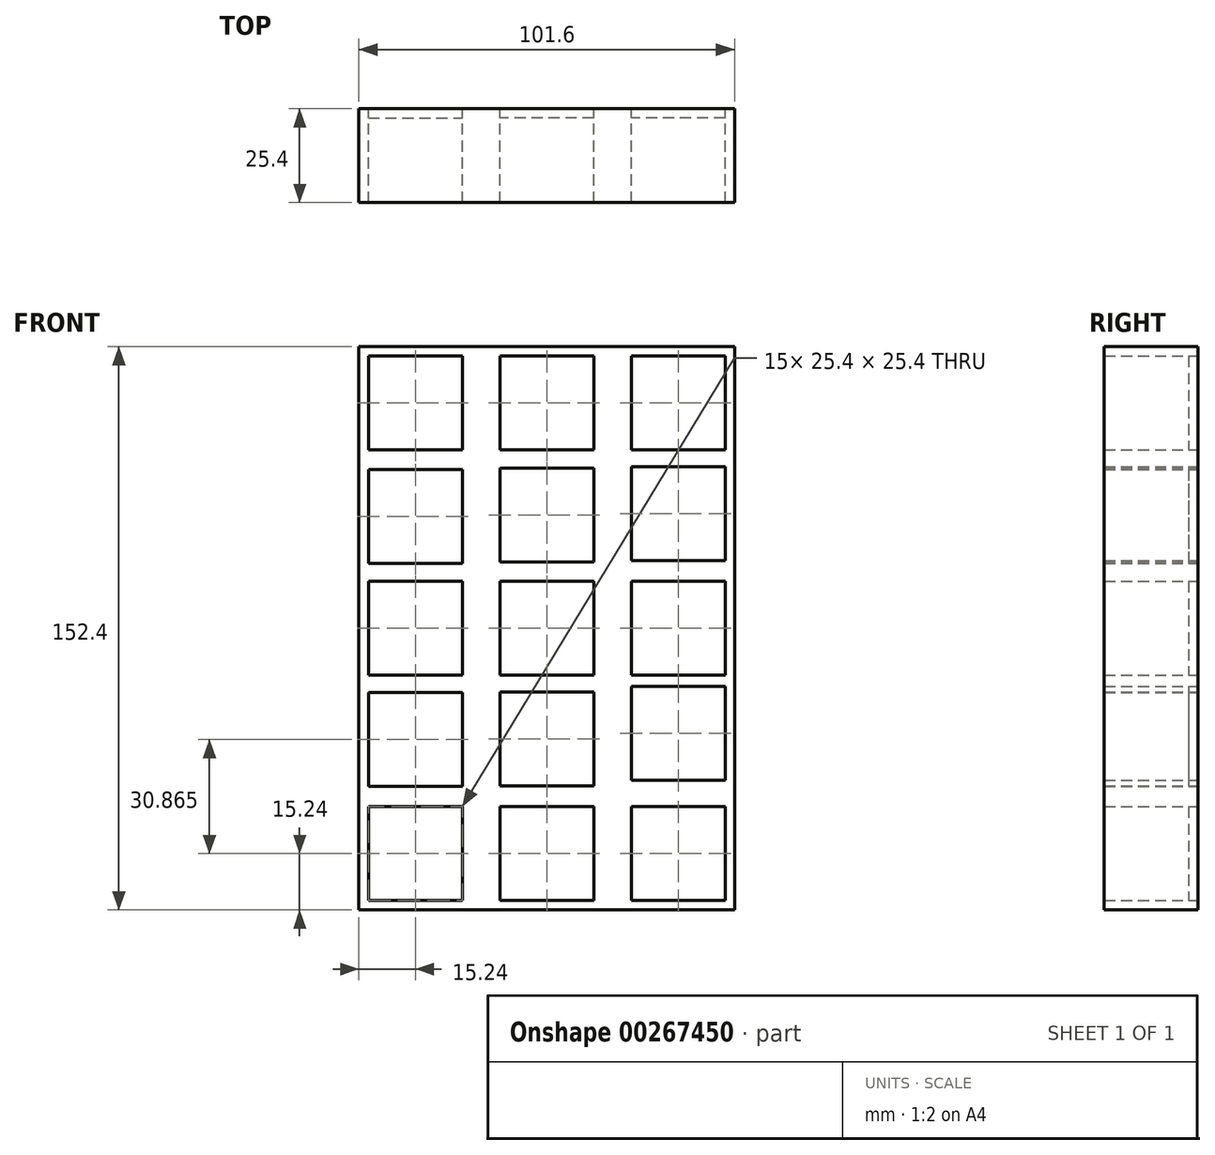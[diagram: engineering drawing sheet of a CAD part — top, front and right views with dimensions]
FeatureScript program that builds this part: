
annotation { "Feature Type Name" : "Feature", "Feature Type Description" : "" }
export const myFeature = defineFeature(function(context is Context, id is Id, definition is map)
    precondition{}
    {
        {
            var Q0;
            Q0=qCreatedBy(makeId("Front.planeOp"),FACE);
            var sketch = newSketch(context, id + "F0", { "sketchPlane" : qUnion([Q0])});
            skLineSegment(sketch, "E0.bottom", {"start": v(50.8, 76.2) * mm, "end": v(-50.8, 76.2) * mm});
            skLineSegment(sketch, "E0.top", {"start": v(50.8, -76.2) * mm, "end": v(-50.8, -76.2) * mm});
            skLineSegment(sketch, "E0.left", {"start": v(50.8, 76.2) * mm, "end": v(50.8, -76.2) * mm});
            skLineSegment(sketch, "E0.right", {"start": v(-50.8, 76.2) * mm, "end": v(-50.8, -76.2) * mm});
            skPoint(sketch, "E0.middle", {"position": v(0, 0) * mm});
            skLineSegment(sketch, "E1.bottom", {"start": v(48.26, 73.66) * mm, "end": v(-48.26, 73.66) * mm});
            skLineSegment(sketch, "E1.top", {"start": v(48.26, -73.66) * mm, "end": v(-48.26, -73.66) * mm});
            skLineSegment(sketch, "E1.left", {"start": v(48.26, 73.66) * mm, "end": v(48.26, -73.66) * mm});
            skLineSegment(sketch, "E1.right", {"start": v(-48.26, 73.66) * mm, "end": v(-48.26, -73.66) * mm});
            skLineSegment(sketch, "E2.bottom", {"start": v(-48.26, 73.66) * mm, "end": v(-22.86, 73.66) * mm});
            skLineSegment(sketch, "E2.top", {"start": v(-48.26, 48.26) * mm, "end": v(-22.86, 48.26) * mm});
            skLineSegment(sketch, "E2.left", {"start": v(-48.26, 73.66) * mm, "end": v(-48.26, 48.26) * mm});
            skLineSegment(sketch, "E2.right", {"start": v(-22.86, 73.66) * mm, "end": v(-22.86, 48.26) * mm});
            skLineSegment(sketch, "E3.bottom", {"start": v(48.26, 73.66) * mm, "end": v(22.86, 73.66) * mm});
            skLineSegment(sketch, "E3.top", {"start": v(48.26, 48.26) * mm, "end": v(22.86, 48.26) * mm});
            skLineSegment(sketch, "E3.left", {"start": v(48.26, 73.66) * mm, "end": v(48.26, 48.26) * mm});
            skLineSegment(sketch, "E3.right", {"start": v(22.86, 73.66) * mm, "end": v(22.86, 48.26) * mm});
            skLineSegment(sketch, "E4", {"start": v(0, 73.66) * mm, "end": v(0, 60.96) * mm});
            skPoint(sketch, "E4.endSnap0", {"position": v(0, 73.66) * mm});
            skLineSegment(sketch, "E5.bottom", {"start": v(12.7, 73.66) * mm, "end": v(-12.7, 73.66) * mm});
            skLineSegment(sketch, "E5.top", {"start": v(12.7, 48.26) * mm, "end": v(-12.7, 48.26) * mm});
            skLineSegment(sketch, "E5.left", {"start": v(12.7, 73.66) * mm, "end": v(12.7, 48.26) * mm});
            skLineSegment(sketch, "E5.right", {"start": v(-12.7, 73.66) * mm, "end": v(-12.7, 48.26) * mm});
            skPoint(sketch, "E5.middle", {"position": v(0, 60.96) * mm});
            skLineSegment(sketch, "E6", {"start": v(0, -73.66) * mm, "end": v(0, -60.96) * mm});
            skPoint(sketch, "E6.endSnap0", {"position": v(0, -73.66) * mm});
            skLineSegment(sketch, "E7.bottom", {"start": v(12.7, -48.26) * mm, "end": v(-12.7, -48.26) * mm});
            skLineSegment(sketch, "E7.top", {"start": v(12.7, -73.66) * mm, "end": v(-12.7, -73.66) * mm});
            skLineSegment(sketch, "E7.left", {"start": v(12.7, -48.26) * mm, "end": v(12.7, -73.66) * mm});
            skLineSegment(sketch, "E7.right", {"start": v(-12.7, -48.26) * mm, "end": v(-12.7, -73.66) * mm});
            skPoint(sketch, "E7.middle", {"position": v(0, -60.96) * mm});
            skLineSegment(sketch, "E8.bottom", {"start": v(-48.26, -73.66) * mm, "end": v(-22.86, -73.66) * mm});
            skLineSegment(sketch, "E8.top", {"start": v(-48.26, -48.26) * mm, "end": v(-22.86, -48.26) * mm});
            skLineSegment(sketch, "E8.left", {"start": v(-48.26, -73.66) * mm, "end": v(-48.26, -48.26) * mm});
            skLineSegment(sketch, "E8.right", {"start": v(-22.86, -73.66) * mm, "end": v(-22.86, -48.26) * mm});
            skLineSegment(sketch, "E9.bottom", {"start": v(48.26, -73.66) * mm, "end": v(22.86, -73.66) * mm});
            skLineSegment(sketch, "E9.top", {"start": v(48.26, -48.26) * mm, "end": v(22.86, -48.26) * mm});
            skLineSegment(sketch, "E9.left", {"start": v(48.26, -73.66) * mm, "end": v(48.26, -48.26) * mm});
            skLineSegment(sketch, "E9.right", {"start": v(22.86, -73.66) * mm, "end": v(22.86, -48.26) * mm});
            skLineSegment(sketch, "E10.bottom", {"start": v(12.7, 12.7) * mm, "end": v(-12.7, 12.7) * mm});
            skLineSegment(sketch, "E10.top", {"start": v(12.7, -12.7) * mm, "end": v(-12.7, -12.7) * mm});
            skLineSegment(sketch, "E10.left", {"start": v(12.7, 12.7) * mm, "end": v(12.7, -12.7) * mm});
            skLineSegment(sketch, "E10.right", {"start": v(-12.7, 12.7) * mm, "end": v(-12.7, -12.7) * mm});
            skLineSegment(sketch, "E11", {"start": v(-48.26, 0) * mm, "end": v(-35.56, 0) * mm});
            skLineSegment(sketch, "E12", {"start": v(48.26, 0) * mm, "end": v(35.56, 0) * mm});
            skLineSegment(sketch, "E13.bottom", {"start": v(-48.26, 12.7) * mm, "end": v(-22.86, 12.7) * mm});
            skLineSegment(sketch, "E13.top", {"start": v(-48.26, -12.7) * mm, "end": v(-22.86, -12.7) * mm});
            skLineSegment(sketch, "E13.left", {"start": v(-48.26, 12.7) * mm, "end": v(-48.26, -12.7) * mm});
            skLineSegment(sketch, "E13.right", {"start": v(-22.86, 12.7) * mm, "end": v(-22.86, -12.7) * mm});
            skPoint(sketch, "E13.middle", {"position": v(-35.56, 0) * mm});
            skLineSegment(sketch, "E14.bottom", {"start": v(48.26, 12.7) * mm, "end": v(22.86, 12.7) * mm});
            skLineSegment(sketch, "E14.top", {"start": v(48.26, -12.7) * mm, "end": v(22.86, -12.7) * mm});
            skLineSegment(sketch, "E14.left", {"start": v(48.26, 12.7) * mm, "end": v(48.26, -12.7) * mm});
            skLineSegment(sketch, "E14.right", {"start": v(22.86, 12.7) * mm, "end": v(22.86, -12.7) * mm});
            skPoint(sketch, "E14.middle", {"position": v(35.56, 0) * mm});
            skLineSegment(sketch, "E15", {"start": v(-48.26, 30.25) * mm, "end": v(-35.56, 30.25) * mm});
            skLineSegment(sketch, "E16.bottom", {"start": v(-22.86, 42.95) * mm, "end": v(-48.26, 42.95) * mm});
            skLineSegment(sketch, "E16.top", {"start": v(-22.86, 17.55) * mm, "end": v(-48.26, 17.55) * mm});
            skLineSegment(sketch, "E16.left", {"start": v(-22.86, 42.95) * mm, "end": v(-22.86, 17.55) * mm});
            skLineSegment(sketch, "E16.right", {"start": v(-48.26, 42.95) * mm, "end": v(-48.26, 17.55) * mm});
            skPoint(sketch, "E16.middle", {"position": v(-35.56, 30.25) * mm});
            skLineSegment(sketch, "E17.bottom", {"start": v(48.26, 43.78) * mm, "end": v(22.86, 43.78) * mm});
            skLineSegment(sketch, "E17.top", {"start": v(48.26, 18.38) * mm, "end": v(22.86, 18.38) * mm});
            skLineSegment(sketch, "E17.left", {"start": v(48.26, 43.78) * mm, "end": v(48.26, 18.38) * mm});
            skLineSegment(sketch, "E17.right", {"start": v(22.86, 43.78) * mm, "end": v(22.86, 18.38) * mm});
            skPoint(sketch, "E17.middle", {"position": v(35.56, 31.08) * mm});
            skPoint(sketch, "E18", {"position": v(0, 30.66) * mm});
            skLineSegment(sketch, "E19.bottom", {"start": v(12.7, 43.36) * mm, "end": v(-12.7, 43.36) * mm});
            skLineSegment(sketch, "E19.top", {"start": v(12.7, 17.96) * mm, "end": v(-12.7, 17.96) * mm});
            skLineSegment(sketch, "E19.left", {"start": v(12.7, 43.36) * mm, "end": v(12.7, 17.96) * mm});
            skLineSegment(sketch, "E19.right", {"start": v(-12.7, 43.36) * mm, "end": v(-12.7, 17.96) * mm});
            skPoint(sketch, "E20", {"position": v(0, -29.93) * mm});
            skLineSegment(sketch, "E21.bottom", {"start": v(12.7, -17.23) * mm, "end": v(-12.7, -17.23) * mm});
            skLineSegment(sketch, "E21.top", {"start": v(12.7, -42.63) * mm, "end": v(-12.7, -42.63) * mm});
            skLineSegment(sketch, "E21.left", {"start": v(12.7, -17.23) * mm, "end": v(12.7, -42.63) * mm});
            skLineSegment(sketch, "E21.right", {"start": v(-12.7, -17.23) * mm, "end": v(-12.7, -42.63) * mm});
            skLineSegment(sketch, "E22", {"start": v(-48.26, -30.1) * mm, "end": v(-35.56, -30.1) * mm});
            skLineSegment(sketch, "E23", {"start": v(48.26, -28.44) * mm, "end": v(35.56, -28.44) * mm});
            skLineSegment(sketch, "E24.bottom", {"start": v(-48.26, -17.4) * mm, "end": v(-22.86, -17.4) * mm});
            skLineSegment(sketch, "E24.top", {"start": v(-48.26, -42.8) * mm, "end": v(-22.86, -42.8) * mm});
            skLineSegment(sketch, "E24.left", {"start": v(-48.26, -17.4) * mm, "end": v(-48.26, -42.8) * mm});
            skLineSegment(sketch, "E24.right", {"start": v(-22.86, -17.4) * mm, "end": v(-22.86, -42.8) * mm});
            skPoint(sketch, "E24.middle", {"position": v(-35.56, -30.1) * mm});
            skLineSegment(sketch, "E25.bottom", {"start": v(48.26, -15.74) * mm, "end": v(22.86, -15.74) * mm});
            skLineSegment(sketch, "E25.top", {"start": v(48.26, -41.14) * mm, "end": v(22.86, -41.14) * mm});
            skLineSegment(sketch, "E25.left", {"start": v(48.26, -15.74) * mm, "end": v(48.26, -41.14) * mm});
            skLineSegment(sketch, "E25.right", {"start": v(22.86, -15.74) * mm, "end": v(22.86, -41.14) * mm});
            skPoint(sketch, "E25.middle", {"position": v(35.56, -28.44) * mm});
            skSolve(sketch);
        }
        {
            var Q0;
            Q0=makeQuery(id+"F0.imprint","IMPRINT",FACE,{"disambiguationData":[TD([[makeQuery(id+"F0.imprint","IMPRINT",EDGE,{"derivedFrom":sQuery(id+"F0.wireOp",EDGE,"E2.bottom")}),-1.0]])]});
            var Q1;
            Q1=makeQuery(id+"F0.imprint","IMPRINT",FACE,{"disambiguationData":[TD([[makeQuery(id+"F0.imprint","IMPRINT",EDGE,{"derivedFrom":sQuery(id+"F0.wireOp",EDGE,"E5.top")}),-1.0]])]});
            var Q2;
            Q2=makeQuery(id+"F0.imprint","IMPRINT",FACE,{"disambiguationData":[TD([[makeQuery(id+"F0.imprint","IMPRINT",EDGE,{"derivedFrom":sQuery(id+"F0.wireOp",EDGE,"E3.bottom")}),1.0]])]});
            var Q3;
            Q3=makeQuery(id+"F0.imprint","IMPRINT",FACE,{"disambiguationData":[TD([[makeQuery(id+"F0.imprint","IMPRINT",EDGE,{"derivedFrom":sQuery(id+"F0.wireOp",EDGE,"E17.bottom")}),1.0]])]});
            var Q4;
            Q4=makeQuery(id+"F0.imprint","IMPRINT",FACE,{"disambiguationData":[TD([[makeQuery(id+"F0.imprint","IMPRINT",EDGE,{"derivedFrom":sQuery(id+"F0.wireOp",EDGE,"E19.bottom")}),1.0]])]});
            var Q5;
            {var subQ2=sQuery(id+"F0.wireOp",EDGE,"E16.bottom");Q5=makeQuery(id+"F0.imprint","IMPRINT",FACE,{"disambiguationData":[TD([[makeQuery(id+"F0.imprint","IMPRINT",EDGE,{"derivedFrom":subQ2}),1.0]])]});}
            var Q6;
            {var subQ4=sQuery(id+"F0.wireOp",EDGE,"E13.bottom");Q6=makeQuery(id+"F0.imprint","IMPRINT",FACE,{"disambiguationData":[TD([[makeQuery(id+"F0.imprint","IMPRINT",EDGE,{"derivedFrom":subQ4}),-1.0]])]});}
            var Q7;
            Q7=makeQuery(id+"F0.imprint","IMPRINT",FACE,{"disambiguationData":[TD([[makeQuery(id+"F0.imprint","IMPRINT",EDGE,{"derivedFrom":sQuery(id+"F0.wireOp",EDGE,"E10.bottom")}),1.0]])]});
            var Q8;
            {var subQ4=sQuery(id+"F0.wireOp",EDGE,"E14.bottom");Q8=makeQuery(id+"F0.imprint","IMPRINT",FACE,{"disambiguationData":[TD([[makeQuery(id+"F0.imprint","IMPRINT",EDGE,{"derivedFrom":subQ4}),1.0]])]});}
            var Q9;
            {var subQ4=sQuery(id+"F0.wireOp",EDGE,"E25.bottom");Q9=makeQuery(id+"F0.imprint","IMPRINT",FACE,{"disambiguationData":[TD([[makeQuery(id+"F0.imprint","IMPRINT",EDGE,{"derivedFrom":subQ4}),1.0]])]});}
            var Q10;
            Q10=makeQuery(id+"F0.imprint","IMPRINT",FACE,{"disambiguationData":[TD([[makeQuery(id+"F0.imprint","IMPRINT",EDGE,{"derivedFrom":sQuery(id+"F0.wireOp",EDGE,"E21.bottom")}),1.0]])]});
            var Q11;
            {var subQ4=sQuery(id+"F0.wireOp",EDGE,"E24.bottom");Q11=makeQuery(id+"F0.imprint","IMPRINT",FACE,{"disambiguationData":[TD([[makeQuery(id+"F0.imprint","IMPRINT",EDGE,{"derivedFrom":subQ4}),-1.0]])]});}
            var Q12;
            Q12=makeQuery(id+"F0.imprint","IMPRINT",FACE,{"disambiguationData":[TD([[makeQuery(id+"F0.imprint","IMPRINT",EDGE,{"derivedFrom":sQuery(id+"F0.wireOp",EDGE,"E8.bottom")}),1.0]])]});
            var Q13;
            Q13=makeQuery(id+"F0.imprint","IMPRINT",FACE,{"disambiguationData":[TD([[makeQuery(id+"F0.imprint","IMPRINT",EDGE,{"derivedFrom":sQuery(id+"F0.wireOp",EDGE,"E7.bottom")}),1.0]])]});
            var Q14;
            Q14=makeQuery(id+"F0.imprint","IMPRINT",FACE,{"disambiguationData":[TD([[makeQuery(id+"F0.imprint","IMPRINT",EDGE,{"derivedFrom":sQuery(id+"F0.wireOp",EDGE,"E9.bottom")}),-1.0]])]});
            extrude(context, id + "F1", {"entities" : qUnion([Q0, Q1, Q2, Q3, Q4, Q5, Q6, Q7, Q8, Q9, Q10, Q11, Q12, Q13, Q14]), "depth" : 2.54 * mm});
        }
        {
            var Q0;
            Q0=makeQuery(id+"F0.imprint","IMPRINT",FACE,{"disambiguationData":[TD([[makeQuery(id+"F0.imprint","IMPRINT",EDGE,{"derivedFrom":sQuery(id+"F0.wireOp",EDGE,"E0.bottom")}),1.0]])]});
            var Q1;
            {var subQ22=sQuery(id+"F0.wireOp",EDGE,"E2.top");Q1=makeQuery(id+"F0.imprint","IMPRINT",FACE,{"disambiguationData":[TD([[makeQuery(id+"F0.imprint","IMPRINT",EDGE,{"derivedFrom":subQ22}),-1.0]])]});}
            extrude(context, id + "F2", {"entities" : qUnion([Q0, Q1]), "depth" : 25.4 * mm});
        }
    });
